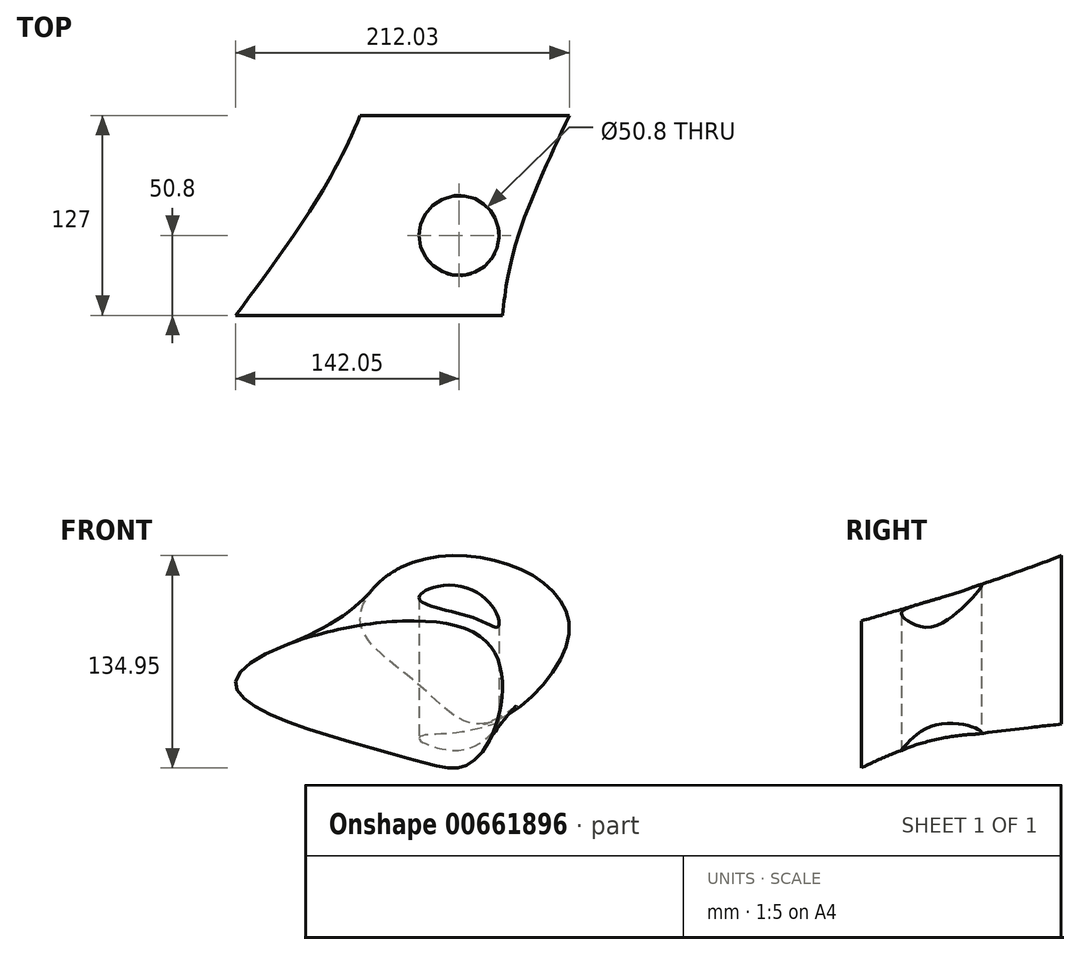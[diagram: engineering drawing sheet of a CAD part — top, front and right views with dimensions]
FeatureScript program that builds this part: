
annotation { "Feature Type Name" : "Feature", "Feature Type Description" : "" }
export const myFeature = defineFeature(function(context is Context, id is Id, definition is map)
    precondition{}
    {
        {
            var Q0;
            Q0=qCreatedBy(makeId("Front.planeOp"),FACE);
            var sketch = newSketch(context, id + "F0", { "sketchPlane" : qUnion([Q0])});
            skFitSpline(sketch, "E0", {"points": [v(-49.93, 43.25) * mm, v(23.9, 43.25) * mm, v(56.96, 0) * mm, v(3.52, -55.9) * mm, v(-37.27, -32) * mm, v(-75.24, 7.38) * mm, v(-49.93, 43.25) * mm]});
            skSolve(sketch);
        }
        {
            var Q0;
            Q0=qCreatedBy(makeId("Front.planeOp"),FACE);
            cPlane(context, id + "F1", {"entities" : qUnion([Q0]), "cplaneType" : CPlaneType.OFFSET, "offset" : 127 * mm, "width" : 152.4 * mm, "height" : 152.4 * mm});
        }
        {
            var Q0;
            Q0=qCreatedBy(id+"F1.planeOp",FACE);
            var sketch = newSketch(context, id + "F2", { "sketchPlane" : qUnion([Q0])});
            skLineSegment(sketch, "E1", {"start": v(-154.4, -27.9) * mm, "end": v(-50.8, -76.2) * mm, "construction": true});
            skLineSegment(sketch, "E2", {"start": v(-50.8, -76.2) * mm, "end": v(-72.65, -45) * mm, "construction": true});
            skLineSegment(sketch, "E3", {"start": v(-127, -76.2) * mm, "end": v(0, -76.2) * mm, "construction": true});
            skFitSpline(sketch, "E4", {"points": [v(0, -76.2) * mm, v(-50.8, -76.2) * mm, v(-154.4, -27.9) * mm, v(0, 0) * mm, v(0, -76.2) * mm]});
            skSolve(sketch);
        }
        {
            var Q0;
            Q0=makeQuery(id+"F0.imprint","IMPRINT",FACE,{"disambiguationData":[TD([[makeQuery(id+"F0.imprint","IMPRINT",EDGE,{"derivedFrom":sQuery(id+"F0.wireOp",EDGE,"E0")}),-1.0]])]});
            var Q1;
            Q1=makeQuery(id+"F2.imprint","IMPRINT",FACE,{"disambiguationData":[TD([[makeQuery(id+"F2.imprint","IMPRINT",EDGE,{"derivedFrom":sQuery(id+"F2.wireOp",EDGE,"E4")}),-1.0]])]});
            loft(context, id + "F3", {"sheetProfilesArray" : [{ "sheetProfileEntities" : qUnion([Q0]) }, { "sheetProfileEntities" : qUnion([Q1]) }]});
        }
        {
            var Q0;
            Q0=qCreatedBy(makeId("Top.planeOp"),FACE);
            var sketch = newSketch(context, id + "F4", { "sketchPlane" : qUnion([Q0])});
            skCircle(sketch, "E5", {"center": v(-12.7, -76.2) * mm, "radius": 25.4 * mm});
            skSolve(sketch);
        }
        {
            var Q0;
            Q0=makeQuery(id+"F4.imprint","IMPRINT",FACE,{"disambiguationData":[TD([[makeQuery(id+"F4.imprint","IMPRINT",EDGE,{"derivedFrom":sQuery(id+"F4.wireOp",EDGE,"E5")}),1.0]])]});
            extrude(context, id + "F5", {"entities" : qUnion([Q0]), "endBound" : BoundingType.SYMMETRIC, "depth" : 254 * mm, "offsetDistance" : 25.4 * mm});
        }
        {
            var Q0;
            Q0=makeQuery(id+"F5.opExtrude","SWEPT_BODY",BODY,{"disambiguationData":[OSD([sQuery(id+"F4.wireOp",EDGE,"E5")])]});
            var Q1;
            Q1=makeQuery(id+"F3.opLoft","SWEPT_BODY",BODY,{"disambiguationData":[OSD([makeQuery(id+"F0.imprint","IMPRINT",FACE,{"disambiguationData":[TD([[makeQuery(id+"F0.imprint","IMPRINT",EDGE,{"derivedFrom":sQuery(id+"F0.wireOp",EDGE,"E0")}),-1.0]])]}),makeQuery(id+"F2.imprint","IMPRINT",FACE,{"disambiguationData":[TD([[makeQuery(id+"F2.imprint","IMPRINT",EDGE,{"derivedFrom":sQuery(id+"F2.wireOp",EDGE,"E4")}),-1.0]])]})])]});
            booleanBodies(context, id + "F6", {"operationType" : BooleanOperationType.SUBTRACTION, "tools" : qUnion([Q0]), "targets" : qUnion([Q1])});
        }
    });
